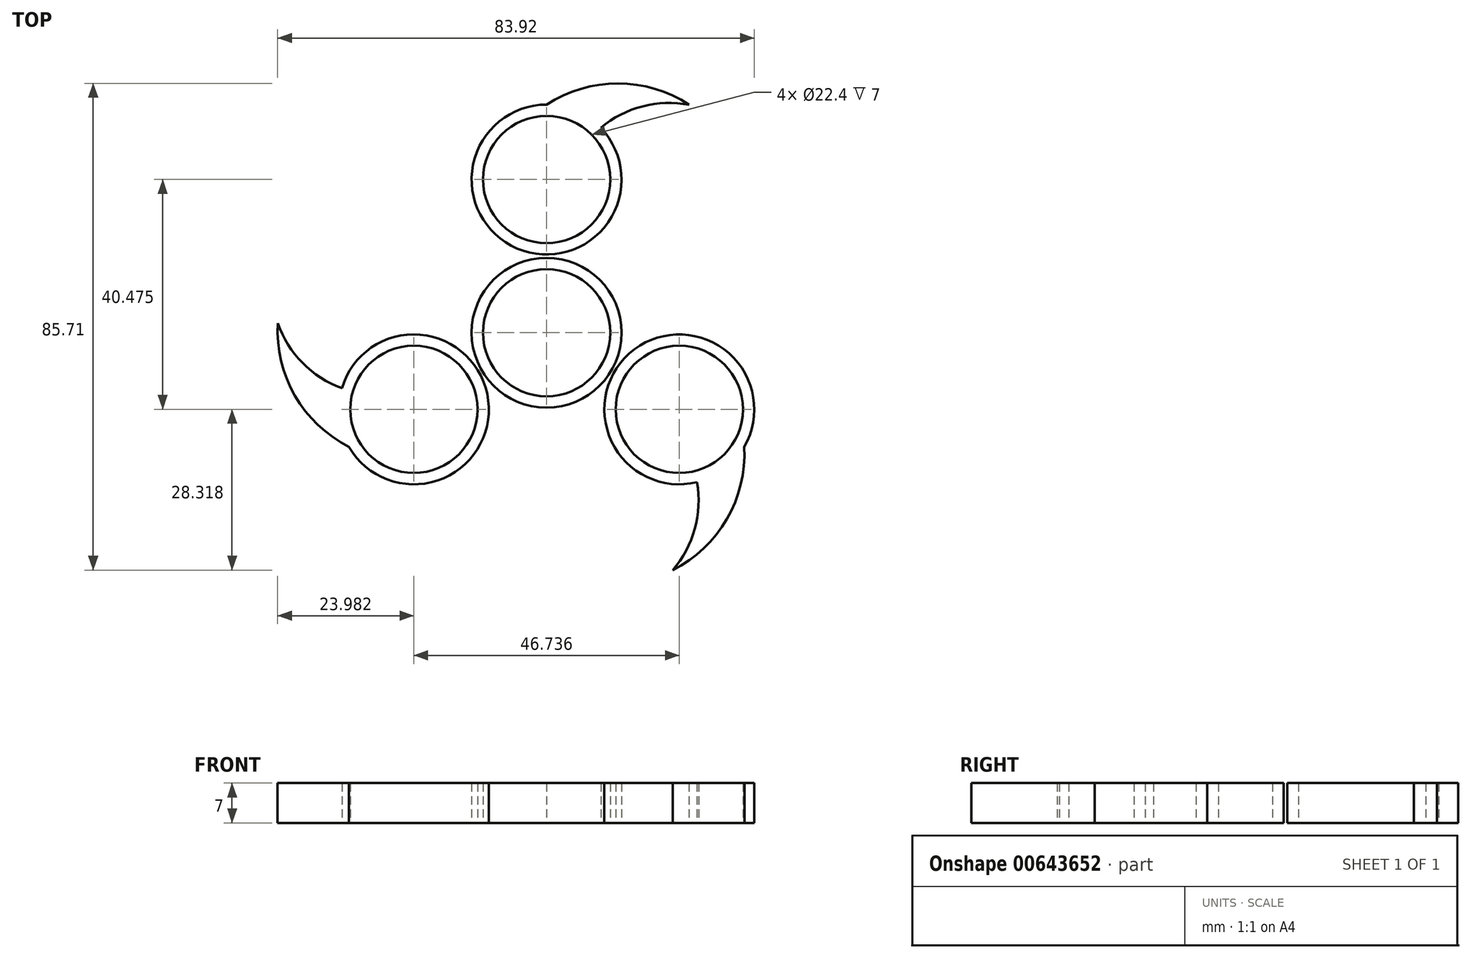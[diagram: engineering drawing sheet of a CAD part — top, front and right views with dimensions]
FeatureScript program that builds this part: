
annotation { "Feature Type Name" : "Feature", "Feature Type Description" : "" }
export const myFeature = defineFeature(function(context is Context, id is Id, definition is map)
    precondition{}
    {
        {
            var Q0;
            Q0=qCreatedBy(makeId("Top.planeOp"),FACE);
            var sketch = newSketch(context, id + "F0", { "sketchPlane" : qUnion([Q0])});
            skCircle(sketch, "E0", {"center": v(0, 0) * mm, "radius": 11.2 * mm});
            skCircle(sketch, "E1", {"center": v(0, 0) * mm, "radius": 13.2 * mm});
            skCircle(sketch, "E2", {"center": v(0, 26.98) * mm, "radius": 11.2 * mm});
            skCircle(sketch, "E3", {"center": v(0, 26.98) * mm, "radius": 13.2 * mm});
            skCircle(sketch, "E4.1.0", {"center": v(-23.37, -13.5) * mm, "radius": 11.2 * mm});
            skCircle(sketch, "E4.1.1", {"center": v(-23.37, -13.5) * mm, "radius": 13.2 * mm});
            skCircle(sketch, "E4.2.0", {"center": v(23.37, -13.5) * mm, "radius": 11.2 * mm});
            skCircle(sketch, "E4.2.1", {"center": v(23.37, -13.5) * mm, "radius": 13.2 * mm});
            skArc(sketch, "E5", {"start": v(25.1, 40.14) * mm, "mid": v(12.56, 43.9) * mm, "end": v(0, 40.18) * mm});
            skArc(sketch, "E6", {"start": v(25.1, 40.14) * mm, "mid": v(16.87, 39.87) * mm, "end": v(9.55, 36.1) * mm});
            skArc(sketch, "E7.1.0", {"start": v(-47.31, 1.67) * mm, "mid": v(-44.3, -11.08) * mm, "end": v(-34.8, -20.1) * mm});
            skArc(sketch, "E7.1.1", {"start": v(-47.31, 1.67) * mm, "mid": v(-42.96, -5.32) * mm, "end": v(-36.04, -9.78) * mm});
            skArc(sketch, "E8.1.2.0", {"start": v(22.2, -41.81) * mm, "mid": v(31.74, -32.83) * mm, "end": v(34.8, -20.1) * mm});
            skArc(sketch, "E8.4.2.0", {"start": v(22.2, -41.81) * mm, "mid": v(26.1, -34.55) * mm, "end": v(26.49, -26.32) * mm});
            skSolve(sketch);
        }
        {
            var Q0;
            Q0=makeQuery(id+"F0.imprint","IMPRINT",FACE,{"disambiguationData":[TD([[makeQuery(id+"F0.imprint","IMPRINT",EDGE,{"derivedFrom":sQuery(id+"F0.wireOp",EDGE,"E2")}),-1.0]])]});
            var Q1;
            Q1=makeQuery(id+"F0.imprint","IMPRINT",FACE,{"disambiguationData":[TD([[makeQuery(id+"F0.imprint","IMPRINT",EDGE,{"derivedFrom":sQuery(id+"F0.wireOp",EDGE,"E4.2.0")}),-1.0]])]});
            var Q2;
            {var subQ0=sQuery(id+"F0.wireOp",EDGE,"E5");Q2=makeQuery(id+"F0.imprint","IMPRINT",FACE,{"disambiguationData":[TD([[makeQuery(id+"F0.imprint","IMPRINT",EDGE,{"derivedFrom":subQ0}),1.0]])]});}
            var Q3;
            Q3=makeQuery(id+"F0.imprint","IMPRINT",FACE,{"disambiguationData":[TD([[makeQuery(id+"F0.imprint","IMPRINT",EDGE,{"derivedFrom":sQuery(id+"F0.wireOp",EDGE,"E4.1.0")}),-1.0]])]});
            var Q4;
            {var subQ0=sQuery(id+"F0.wireOp",EDGE,"E7.1.0");Q4=makeQuery(id+"F0.imprint","IMPRINT",FACE,{"disambiguationData":[TD([[makeQuery(id+"F0.imprint","IMPRINT",EDGE,{"derivedFrom":subQ0}),1.0]])]});}
            var Q5;
            {var subQ0=sQuery(id+"F0.wireOp",EDGE,"E8.1.2.0");Q5=makeQuery(id+"F0.imprint","IMPRINT",FACE,{"disambiguationData":[TD([[makeQuery(id+"F0.imprint","IMPRINT",EDGE,{"derivedFrom":subQ0}),1.0]])]});}
            var Q6;
            Q6=makeQuery(id+"F0.imprint","IMPRINT",FACE,{"disambiguationData":[TD([[makeQuery(id+"F0.imprint","IMPRINT",EDGE,{"derivedFrom":sQuery(id+"F0.wireOp",EDGE,"E0")}),-1.0]])]});
            extrude(context, id + "F1", {"entities" : qUnion([Q0, Q1, Q2, Q3, Q4, Q5, Q6]), "depth" : 7 * mm, "offsetDistance" : 25 * mm});
        }
    });
